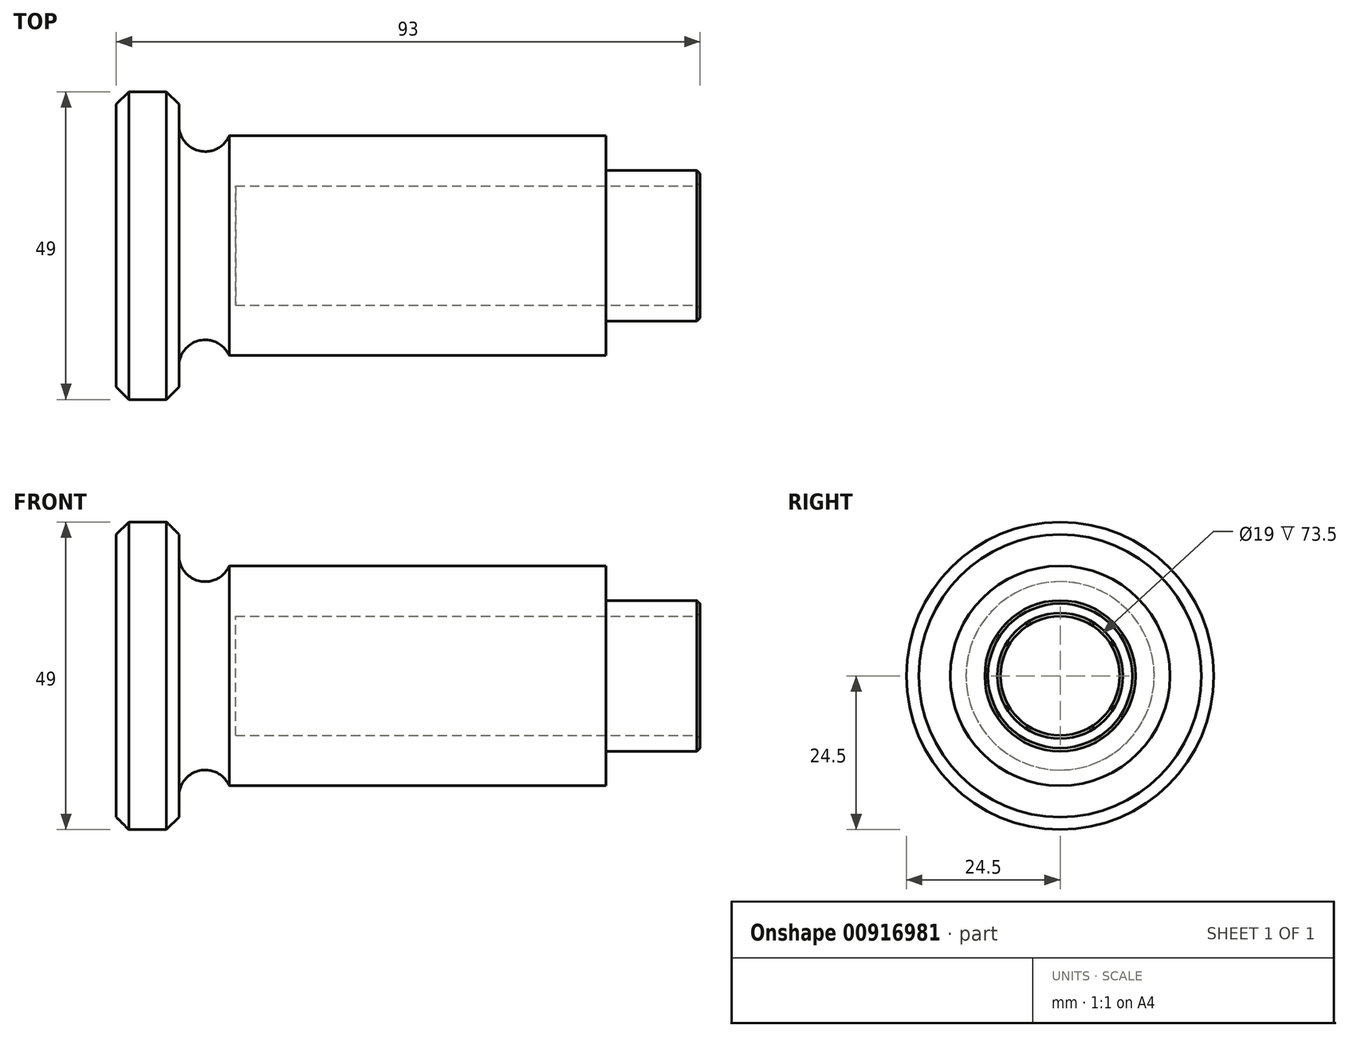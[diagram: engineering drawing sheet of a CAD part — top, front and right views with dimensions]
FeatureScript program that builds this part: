
annotation { "Feature Type Name" : "Feature", "Feature Type Description" : "" }
export const myFeature = defineFeature(function(context is Context, id is Id, definition is map)
    precondition{}
    {
        {
            var Q0;
            Q0=qCreatedBy(makeId("Front.planeOp"),FACE);
            var sketch = newSketch(context, id + "F0", { "sketchPlane" : qUnion([Q0])});
            skLineSegment(sketch, "E0", {"start": v(0, 0) * mm, "end": v(0, 24.5) * mm});
            skLineSegment(sketch, "E1", {"start": v(0, 24.5) * mm, "end": v(10, 24.5) * mm});
            skLineSegment(sketch, "E2", {"start": v(10, 24.5) * mm, "end": v(10, 15) * mm});
            skLineSegment(sketch, "E3", {"start": v(10, 15) * mm, "end": v(18, 15) * mm});
            skLineSegment(sketch, "E4", {"start": v(18, 15) * mm, "end": v(18, 17.5) * mm});
            skLineSegment(sketch, "E5", {"start": v(18, 17.5) * mm, "end": v(78, 17.5) * mm});
            skLineSegment(sketch, "E6", {"start": v(78, 17.5) * mm, "end": v(78, 12) * mm});
            skLineSegment(sketch, "E7", {"start": v(78, 12) * mm, "end": v(93, 12) * mm});
            skLineSegment(sketch, "E8", {"start": v(93, 12) * mm, "end": v(93, 9.5) * mm});
            skLineSegment(sketch, "E9.0", {"start": v(93, 9.5) * mm, "end": v(19, 9.5) * mm});
            skLineSegment(sketch, "E10", {"start": v(19, 9.5) * mm, "end": v(19, 0) * mm});
            skLineSegment(sketch, "E11", {"start": v(19, 0) * mm, "end": v(0, 0) * mm});
            skPoint(sketch, "E12.orphan", {"position": v(93, 0) * mm});
            skSolve(sketch);
        }
        {
            var Q0;
            Q0=makeQuery(id+"F0.imprint","IMPRINT",FACE,{"disambiguationData":[TD([[makeQuery(id+"F0.imprint","IMPRINT",EDGE,{"derivedFrom":sQuery(id+"F0.wireOp",EDGE,"E0")}),-1.0]])]});
            var Q1;
            Q1=sQuery(id+"F0.wireOp",EDGE,"E11");
            revolve(context, id + "F1", {"surfaceOperationType" : NewSurfaceOperationType.NEW, "entities" : qUnion([Q0]), "axis" : qUnion([Q1]), "revolveType" : RevolveType.FULL});
        }
        {
            var Q0;
            Q0=makeQuery(id+"F1.opRevolve","SWEPT_EDGE",EDGE,{"disambiguationData":[OSD([sQuery(id+"F0.wireOp",EDGE,"E2"),sQuery(id+"F0.wireOp",EDGE,"E3")])]});
            var Q1;
            Q1=makeQuery(id+"F1.opRevolve","SWEPT_EDGE",EDGE,{"disambiguationData":[OSD([sQuery(id+"F0.wireOp",EDGE,"E3"),sQuery(id+"F0.wireOp",EDGE,"E4")])]});
            fillet(context, id + "F2", {"entities" : qUnion([Q0, Q1]), "radius" : 4.15 * mm, "allowEdgeOverflow" : false});
        }
        {
            var Q0;
            Q0=makeQuery(id+"F1.opRevolve","SWEPT_EDGE",EDGE,{"disambiguationData":[OSD([sQuery(id+"F0.wireOp",EDGE,"E0"),sQuery(id+"F0.wireOp",EDGE,"E1")])]});
            var Q1;
            Q1=makeQuery(id+"F1.opRevolve","SWEPT_EDGE",EDGE,{"disambiguationData":[OSD([sQuery(id+"F0.wireOp",EDGE,"E1"),sQuery(id+"F0.wireOp",EDGE,"E2")])]});
            chamfer(context, id + "F3", {"entities" : qUnion([Q0, Q1]), "width" : 2 * mm, "tangentPropagation" : true});
        }
        {
            var Q0;
            Q0=makeQuery(id+"F1.opRevolve","SWEPT_EDGE",EDGE,{"disambiguationData":[OSD([sQuery(id+"F0.wireOp",EDGE,"E7"),sQuery(id+"F0.wireOp",EDGE,"E8")])]});
            var Q1;
            Q1=makeQuery(id+"F1.opRevolve","SWEPT_EDGE",EDGE,{"disambiguationData":[OSD([sQuery(id+"F0.wireOp",EDGE,"E8"),sQuery(id+"F0.wireOp",EDGE,"E9.0")])]});
            chamfer(context, id + "F4", {"entities" : qUnion([Q0, Q1]), "width" : .5 * mm, "tangentPropagation" : true});
        }
    });
